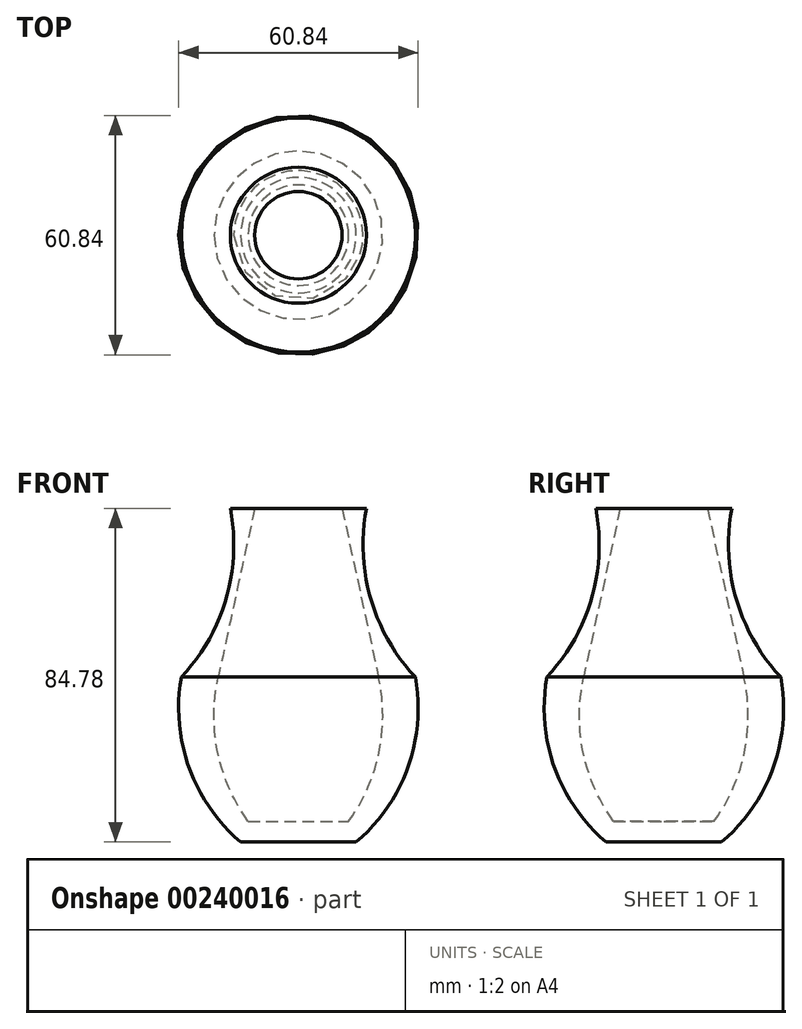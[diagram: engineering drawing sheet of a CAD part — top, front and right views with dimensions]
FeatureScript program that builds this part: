
annotation { "Feature Type Name" : "Feature", "Feature Type Description" : "" }
export const myFeature = defineFeature(function(context is Context, id is Id, definition is map)
    precondition{}
    {
        {
            var Q0;
            Q0=qCreatedBy(makeId("Front.planeOp"),FACE);
            var sketch = newSketch(context, id + "F0", { "sketchPlane" : qUnion([Q0])});
            skLineSegment(sketch, "E0", {"start": v(14.66, -59.16) * mm, "end": v(-16.1, -59.16) * mm});
            skArc(sketch, "E1", {"start": v(14.66, -59.16) * mm, "mid": v(27.79, -40.22) * mm, "end": v(29.72, -17.26) * mm});
            skArc(sketch, "E2", {"start": v(17.28, 25.62) * mm, "mid": v(18.37, 2.69) * mm, "end": v(29.72, -17.26) * mm});
            skLineSegment(sketch, "E3", {"start": v(17.28, 25.62) * mm, "end": v(0, 25.62) * mm});
            skLineSegment(sketch, "E4", {"start": v(0, -59.16) * mm, "end": v(0, 25.62) * mm});
            skSolve(sketch);
        }
        {
            var Q0;
            {var subQ0=sQuery(id+"F0.wireOp",EDGE,"E1");Q0=makeQuery(id+"F0.imprint","IMPRINT",FACE,{"disambiguationData":[TD([[makeQuery(id+"F0.imprint","IMPRINT",EDGE,{"derivedFrom":subQ0}),1.0]])]});}
            var Q1;
            Q1=sQuery(id+"F0.wireOp",EDGE,"E4");
            revolve(context, id + "F1", {"entities" : qUnion([Q0]), "axis" : qUnion([Q1]), "revolveType" : RevolveType.FULL});
        }
        {
            var Q0;
            Q0=qCreatedBy(makeId("Front.planeOp"),FACE);
            var sketch = newSketch(context, id + "F2", { "sketchPlane" : qUnion([Q0])});
            skLineSegment(sketch, "E5", {"start": v(-11.04, 25.89) * mm, "end": v(-20.4, -17.46) * mm});
            skArc(sketch, "E6", {"start": v(-20.4, -17.46) * mm, "mid": v(-20.46, -36.48) * mm, "end": v(-12.77, -53.88) * mm});
            skLineSegment(sketch, "E7", {"start": v(-12.77, -53.88) * mm, "end": v(0, -53.88) * mm});
            skLineSegment(sketch, "E8", {"start": v(-11.04, 25.89) * mm, "end": v(0, 25.89) * mm});
            skLineSegment(sketch, "E9", {"start": v(0, 25.89) * mm, "end": v(0, -53.88) * mm});
            skSolve(sketch);
        }
        {
            var Q0;
            Q0 = qSketchRegion(id + "F2", true);
            var Q1;
            Q1=sQuery(id+"F2.wireOp",EDGE,"E9");
            revolve(context, id + "F3", {"operationType" : NewBodyOperationType.REMOVE, "entities" : qUnion([Q0]), "axis" : qUnion([Q1]), "revolveType" : RevolveType.FULL, "oppositeDirection" : true});
        }
    });
